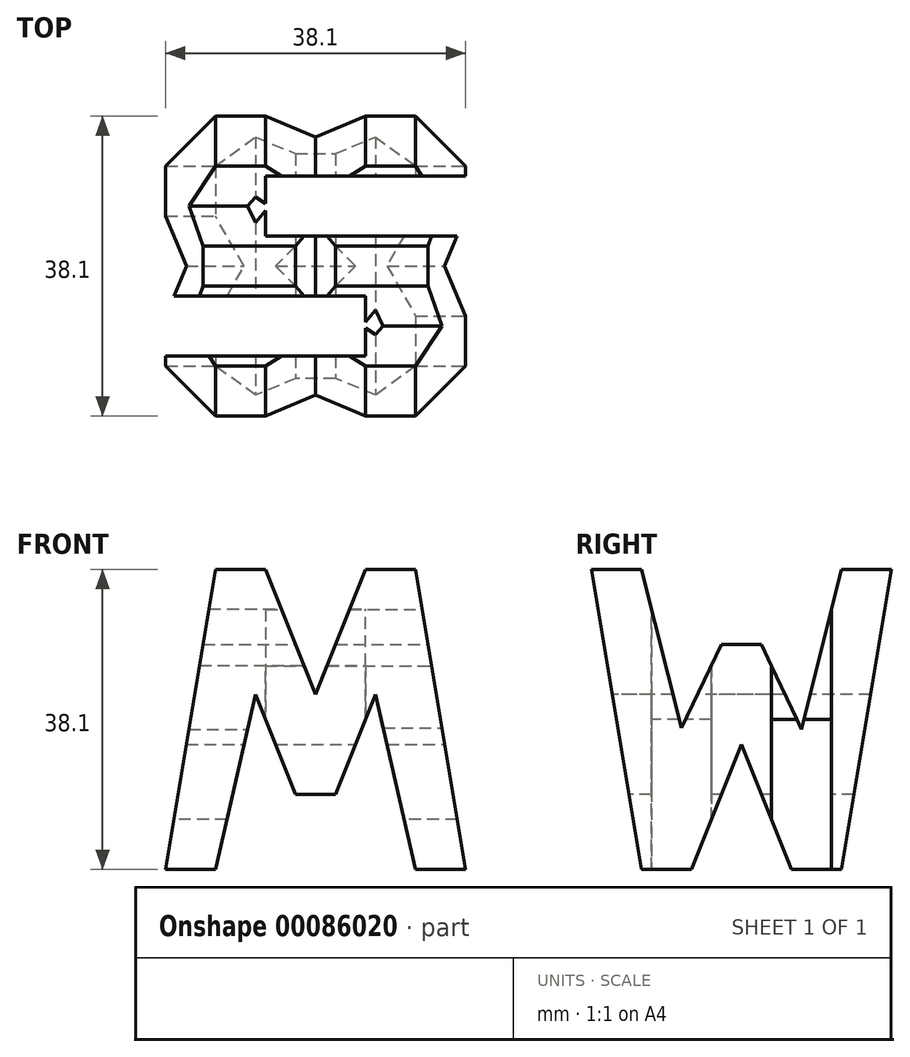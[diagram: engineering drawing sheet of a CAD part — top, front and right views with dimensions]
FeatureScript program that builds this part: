
annotation { "Feature Type Name" : "Feature", "Feature Type Description" : "" }
export const myFeature = defineFeature(function(context is Context, id is Id, definition is map)
    precondition{}
    {
        {
            var Q0;
            Q0=qCreatedBy(makeId("Front.planeOp"),FACE);
            var sketch = newSketch(context, id + "F0", { "sketchPlane" : qUnion([Q0])});
            skLineSegment(sketch, "E0", {"start": v(0, 0) * mm, "end": v(0, 38.1) * mm});
            skLineSegment(sketch, "E1", {"start": v(0, 38.1) * mm, "end": v(38.1, 38.1) * mm});
            skLineSegment(sketch, "E2", {"start": v(38.1, 38.1) * mm, "end": v(38.1, 0) * mm});
            skLineSegment(sketch, "E3", {"start": v(38.1, 0) * mm, "end": v(0, 0) * mm});
            skSolve(sketch);
        }
        {
            var Q0;
            Q0=makeQuery(id+"F0.imprint","IMPRINT",FACE,{"disambiguationData":[TD([[makeQuery(id+"F0.imprint","IMPRINT",EDGE,{"derivedFrom":sQuery(id+"F0.wireOp",EDGE,"E0")}),-1.0]])]});
            extrude(context, id + "F1", {"entities" : qUnion([Q0]), "depth" : 38.1 * mm});
        }
        {
            var Q0;
            Q0=qCreatedBy(makeId("Front.planeOp"),FACE);
            cPlane(context, id + "F2", {"entities" : qUnion([Q0]), "cplaneType" : CPlaneType.OFFSET, "offset" : 38.1 * mm, "width" : 152.4 * mm, "height" : 152.4 * mm});
        }
        {
            var Q0;
            Q0=qCreatedBy(makeId("Top.planeOp"),FACE);
            cPlane(context, id + "F3", {"entities" : qUnion([Q0]), "cplaneType" : CPlaneType.OFFSET, "offset" : 38.1 * mm, "width" : 152.4 * mm, "height" : 152.4 * mm});
        }
        {
            var Q0;
            Q0=qCreatedBy(makeId("Right.planeOp"),FACE);
            cPlane(context, id + "F4", {"entities" : qUnion([Q0]), "cplaneType" : CPlaneType.OFFSET, "offset" : 38.1 * mm, "width" : 152.4 * mm, "height" : 152.4 * mm});
        }
        {
            var Q0;
            Q0=qCreatedBy(id+"F4.planeOp",FACE);
            var sketch = newSketch(context, id + "F5", { "sketchPlane" : qUnion([Q0])});
            skLineSegment(sketch, "E4", {"start": v(-38.1, 38.1) * mm, "end": v(-31.75, 0) * mm});
            skLineSegment(sketch, "E5", {"start": v(-31.75, 0) * mm, "end": v(-25.4, 0) * mm});
            skLineSegment(sketch, "E6", {"start": v(-25.4, 0) * mm, "end": v(-19.05, 15.88) * mm});
            skLineSegment(sketch, "E7", {"start": v(-19.05, 15.88) * mm, "end": v(-12.7, 0) * mm});
            skLineSegment(sketch, "E8", {"start": v(-12.7, 0) * mm, "end": v(-6.35, 0) * mm});
            skLineSegment(sketch, "E9", {"start": v(-11.43, 17.78) * mm, "end": v(-16.51, 28.58) * mm});
            skLineSegment(sketch, "E10", {"start": v(-16.51, 28.58) * mm, "end": v(-21.6, 28.58) * mm});
            skLineSegment(sketch, "E11", {"start": v(-21.6, 28.58) * mm, "end": v(-26.67, 17.95) * mm});
            skLineSegment(sketch, "E12", {"start": v(-26.67, 17.95) * mm, "end": v(-31.75, 38.1) * mm});
            skLineSegment(sketch, "E13", {"start": v(-31.75, 38.1) * mm, "end": v(-38.1, 38.1) * mm});
            skLineSegment(sketch, "E14", {"start": v(-6.35, 0) * mm, "end": v(0, 38.1) * mm});
            skLineSegment(sketch, "E15", {"start": v(0, 38.1) * mm, "end": v(-6.35, 38.1) * mm});
            skLineSegment(sketch, "E16", {"start": v(-6.35, 38.1) * mm, "end": v(-11.43, 17.78) * mm});
            skLineSegment(sketch, "E17.bottom", {"start": v(0, 0) * mm, "end": v(-38.1, 0) * mm});
            skLineSegment(sketch, "E17.top", {"start": v(0, 38.1) * mm, "end": v(-38.1, 38.1) * mm});
            skLineSegment(sketch, "E17.left", {"start": v(0, 0) * mm, "end": v(0, 38.1) * mm});
            skLineSegment(sketch, "E17.right", {"start": v(-38.1, 0) * mm, "end": v(-38.1, 38.1) * mm});
            skSolve(sketch);
        }
        {
            var Q0;
            {var subQ0=sQuery(id+"F5.wireOp",EDGE,"E4");Q0=makeQuery(id+"F5.imprint","IMPRINT",FACE,{"disambiguationData":[TD([[makeQuery(id+"F5.imprint","IMPRINT",EDGE,{"derivedFrom":subQ0}),-1.0]])]});}
            var Q1;
            {var subQ0=sQuery(id+"F5.wireOp",EDGE,"E6");Q1=makeQuery(id+"F5.imprint","IMPRINT",FACE,{"disambiguationData":[TD([[makeQuery(id+"F5.imprint","IMPRINT",EDGE,{"derivedFrom":subQ0}),-1.0]])]});}
            var Q2;
            {var subQ0=sQuery(id+"F5.wireOp",EDGE,"E14");Q2=makeQuery(id+"F5.imprint","IMPRINT",FACE,{"disambiguationData":[TD([[makeQuery(id+"F5.imprint","IMPRINT",EDGE,{"derivedFrom":subQ0}),-1.0]])]});}
            var Q3;
            Q3=makeQuery(id+"F5.imprint","IMPRINT",FACE,{"disambiguationData":[TD([[makeQuery(id+"F5.imprint","IMPRINT",EDGE,{"derivedFrom":sQuery(id+"F5.wireOp",EDGE,"E9")}),-1.0]])]});
            extrude(context, id + "F6", {"entities" : qUnion([Q0, Q1, Q2, Q3]), "operationType" : NewBodyOperationType.REMOVE, "oppositeDirection" : true, "depth" : 38.1 * mm});
        }
        {
            var Q0;
            Q0=qCreatedBy(id+"F2.planeOp",FACE);
            var sketch = newSketch(context, id + "F7", { "sketchPlane" : qUnion([Q0])});
            skLineSegment(sketch, "E18.bottom", {"start": v(0, 38.1) * mm, "end": v(38.1, 38.1) * mm});
            skLineSegment(sketch, "E18.top", {"start": v(0, 0) * mm, "end": v(38.1, 0) * mm});
            skLineSegment(sketch, "E18.left", {"start": v(0, 38.1) * mm, "end": v(0, 0) * mm});
            skLineSegment(sketch, "E18.right", {"start": v(38.1, 38.1) * mm, "end": v(38.1, 0) * mm});
            skLineSegment(sketch, "E19", {"start": v(0, 0) * mm, "end": v(6.35, 38.1) * mm});
            skLineSegment(sketch, "E20", {"start": v(6.35, 38.1) * mm, "end": v(12.7, 38.1) * mm});
            skLineSegment(sketch, "E21", {"start": v(12.7, 38.1) * mm, "end": v(19.05, 22.23) * mm});
            skLineSegment(sketch, "E22", {"start": v(19.05, 22.22) * mm, "end": v(25.4, 38.1) * mm});
            skLineSegment(sketch, "E23", {"start": v(25.4, 38.1) * mm, "end": v(31.75, 38.1) * mm});
            skLineSegment(sketch, "E24", {"start": v(31.75, 38.1) * mm, "end": v(38.1, 0) * mm});
            skLineSegment(sketch, "E25", {"start": v(31.75, 0) * mm, "end": v(26.67, 22.23) * mm});
            skLineSegment(sketch, "E26", {"start": v(26.67, 22.23) * mm, "end": v(21.59, 9.53) * mm});
            skLineSegment(sketch, "E27", {"start": v(21.6, 9.53) * mm, "end": v(16.51, 9.53) * mm});
            skLineSegment(sketch, "E28", {"start": v(16.51, 9.53) * mm, "end": v(11.43, 22.23) * mm});
            skLineSegment(sketch, "E29", {"start": v(11.43, 22.23) * mm, "end": v(6.35, 0) * mm});
            skLineSegment(sketch, "E30", {"start": v(6.35, 0) * mm, "end": v(0, 0) * mm});
            skSolve(sketch);
        }
        {
            var Q0;
            {var subQ0=sQuery(id+"F7.wireOp",EDGE,"E21");Q0=makeQuery(id+"F7.imprint","IMPRINT",FACE,{"disambiguationData":[TD([[makeQuery(id+"F7.imprint","IMPRINT",EDGE,{"derivedFrom":subQ0}),1.0]])]});}
            var Q1;
            {var subQ0=sQuery(id+"F7.wireOp",EDGE,"E19");Q1=makeQuery(id+"F7.imprint","IMPRINT",FACE,{"disambiguationData":[TD([[makeQuery(id+"F7.imprint","IMPRINT",EDGE,{"derivedFrom":subQ0}),1.0]])]});}
            var Q2;
            {var subQ0=sQuery(id+"F7.wireOp",EDGE,"E25");Q2=makeQuery(id+"F7.imprint","IMPRINT",FACE,{"disambiguationData":[TD([[makeQuery(id+"F7.imprint","IMPRINT",EDGE,{"derivedFrom":subQ0}),1.0]])]});}
            var Q3;
            {var subQ0=sQuery(id+"F7.wireOp",EDGE,"E24");Q3=makeQuery(id+"F7.imprint","IMPRINT",FACE,{"disambiguationData":[TD([[makeQuery(id+"F7.imprint","IMPRINT",EDGE,{"derivedFrom":subQ0}),1.0]])]});}
            extrude(context, id + "F8", {"entities" : qUnion([Q0, Q1, Q2, Q3]), "operationType" : NewBodyOperationType.REMOVE, "oppositeDirection" : true, "depth" : 38.1 * mm});
        }
        {
            var Q0;
            Q0=qCreatedBy(makeId("Top.planeOp"),FACE);
            var sketch = newSketch(context, id + "F9", { "sketchPlane" : qUnion([Q0])});
            skLineSegment(sketch, "E31.bottom", {"start": v(0, 0) * mm, "end": v(38.1, 0) * mm});
            skLineSegment(sketch, "E31.top", {"start": v(0, -38.1) * mm, "end": v(38.1, -38.1) * mm});
            skLineSegment(sketch, "E31.left", {"start": v(0, 0) * mm, "end": v(0, -38.1) * mm});
            skLineSegment(sketch, "E31.right", {"start": v(38.1, 0) * mm, "end": v(38.1, -38.1) * mm});
            skLineSegment(sketch, "E32", {"start": v(38.1, -7.62) * mm, "end": v(12.7, -7.62) * mm});
            skLineSegment(sketch, "E33", {"start": v(12.7, -7.62) * mm, "end": v(12.7, -15.24) * mm});
            skLineSegment(sketch, "E34", {"start": v(12.7, -15.24) * mm, "end": v(38.1, -15.24) * mm});
            skLineSegment(sketch, "E35", {"start": v(0, -22.86) * mm, "end": v(25.4, -22.86) * mm});
            skLineSegment(sketch, "E36", {"start": v(25.4, -22.86) * mm, "end": v(25.4, -30.48) * mm});
            skLineSegment(sketch, "E37", {"start": v(25.4, -30.48) * mm, "end": v(0, -30.48) * mm});
            skLineSegment(sketch, "E38.bottom", {"start": v(12.7, -7.62) * mm, "end": v(38.1, -7.62) * mm});
            skLineSegment(sketch, "E38.right", {"start": v(38.1, -7.62) * mm, "end": v(38.1, -15.24) * mm});
            skLineSegment(sketch, "E39.bottom", {"start": v(25.4, -22.86) * mm, "end": v(0, -22.86) * mm});
            skLineSegment(sketch, "E39.right", {"start": v(0, -22.86) * mm, "end": v(0, -30.48) * mm});
            skLineSegment(sketch, "E40.left", {"start": v(0, -38.1) * mm, "end": v(0, 0) * mm});
            skLineSegment(sketch, "E40.right", {"start": v(38.1, -38.1) * mm, "end": v(38.1, 0) * mm});
            skLineSegment(sketch, "E41.bottom", {"start": v(0, -30.48) * mm, "end": v(25.4, -30.48) * mm});
            skLineSegment(sketch, "E41.left", {"start": v(0, -30.48) * mm, "end": v(0, -22.86) * mm});
            skLineSegment(sketch, "E41.right", {"start": v(25.4, -30.48) * mm, "end": v(25.4, -22.86) * mm});
            skLineSegment(sketch, "E42.left", {"start": v(12.7, -15.24) * mm, "end": v(12.7, -7.62) * mm});
            skLineSegment(sketch, "E42.right", {"start": v(38.1, -15.24) * mm, "end": v(38.1, -7.62) * mm});
            skSolve(sketch);
        }
        {
            var Q0;
            Q0=makeQuery(id+"F9.imprint","IMPRINT",FACE,{"disambiguationData":[TD([[makeQuery(id+"F9.imprint","IMPRINT",EDGE,{"derivedFrom":sQuery(id+"F9.wireOp",EDGE,"E41.bottom")}),1.0]])]});
            var Q1;
            Q1=makeQuery(id+"F9.imprint","IMPRINT",FACE,{"disambiguationData":[TD([[makeQuery(id+"F9.imprint","IMPRINT",EDGE,{"derivedFrom":sQuery(id+"F9.wireOp",EDGE,"E34")}),1.0]])]});
            extrude(context, id + "F10", {"entities" : qUnion([Q0, Q1]), "operationType" : NewBodyOperationType.REMOVE, "oppositeDirection" : true, "depth" : 38.1 * mm});
        }
        {
            var Q0;
            Q0=qCreatedBy(id+"F3.planeOp",FACE);
            var sketch = newSketch(context, id + "F11", { "sketchPlane" : qUnion([Q0])});
            skLineSegment(sketch, "E43.bottom", {"start": v(0, 0) * mm, "end": v(38.1, 0) * mm});
            skLineSegment(sketch, "E43.top", {"start": v(0, -38.1) * mm, "end": v(38.1, -38.1) * mm});
            skLineSegment(sketch, "E43.left", {"start": v(0, 0) * mm, "end": v(0, -38.1) * mm});
            skLineSegment(sketch, "E43.right", {"start": v(38.1, 0) * mm, "end": v(38.1, -38.1) * mm});
            skLineSegment(sketch, "E44.bottom", {"start": v(12.7, -7.62) * mm, "end": v(38.1, -7.62) * mm});
            skLineSegment(sketch, "E44.top", {"start": v(12.7, -15.24) * mm, "end": v(38.1, -15.24) * mm});
            skLineSegment(sketch, "E44.left", {"start": v(12.7, -7.62) * mm, "end": v(12.7, -15.24) * mm});
            skLineSegment(sketch, "E44.right", {"start": v(38.1, -7.62) * mm, "end": v(38.1, -15.24) * mm});
            skLineSegment(sketch, "E45.bottom", {"start": v(0, -22.86) * mm, "end": v(25.4, -22.86) * mm});
            skLineSegment(sketch, "E45.top", {"start": v(0, -30.48) * mm, "end": v(25.4, -30.48) * mm});
            skLineSegment(sketch, "E45.left", {"start": v(0, -22.86) * mm, "end": v(0, -30.48) * mm});
            skLineSegment(sketch, "E45.right", {"start": v(25.4, -22.86) * mm, "end": v(25.4, -30.48) * mm});
            skLineSegment(sketch, "E46.bottom", {"start": v(0, -38.1) * mm, "end": v(0, -38.1) * mm});
            skLineSegment(sketch, "E46.top", {"start": v(0, -30.48) * mm, "end": v(0, -30.48) * mm});
            skLineSegment(sketch, "E46.left", {"start": v(0, -38.1) * mm, "end": v(0, -30.48) * mm});
            skLineSegment(sketch, "E46.right", {"start": v(0, -38.1) * mm, "end": v(0, -30.48) * mm});
            skSolve(sketch);
        }
        {
            var Q0;
            Q0=makeQuery(id+"F11.imprint","IMPRINT",FACE,{"disambiguationData":[TD([[makeQuery(id+"F11.imprint","IMPRINT",EDGE,{"derivedFrom":sQuery(id+"F11.wireOp",EDGE,"E45.bottom")}),-1.0]])]});
            var Q1;
            Q1=makeQuery(id+"F11.imprint","IMPRINT",FACE,{"disambiguationData":[TD([[makeQuery(id+"F11.imprint","IMPRINT",EDGE,{"derivedFrom":sQuery(id+"F11.wireOp",EDGE,"E44.bottom")}),-1.0]])]});
            extrude(context, id + "F12", {"entities" : qUnion([Q0, Q1]), "operationType" : NewBodyOperationType.REMOVE, "oppositeDirection" : true, "depth" : 38.1 * mm});
        }
    });
